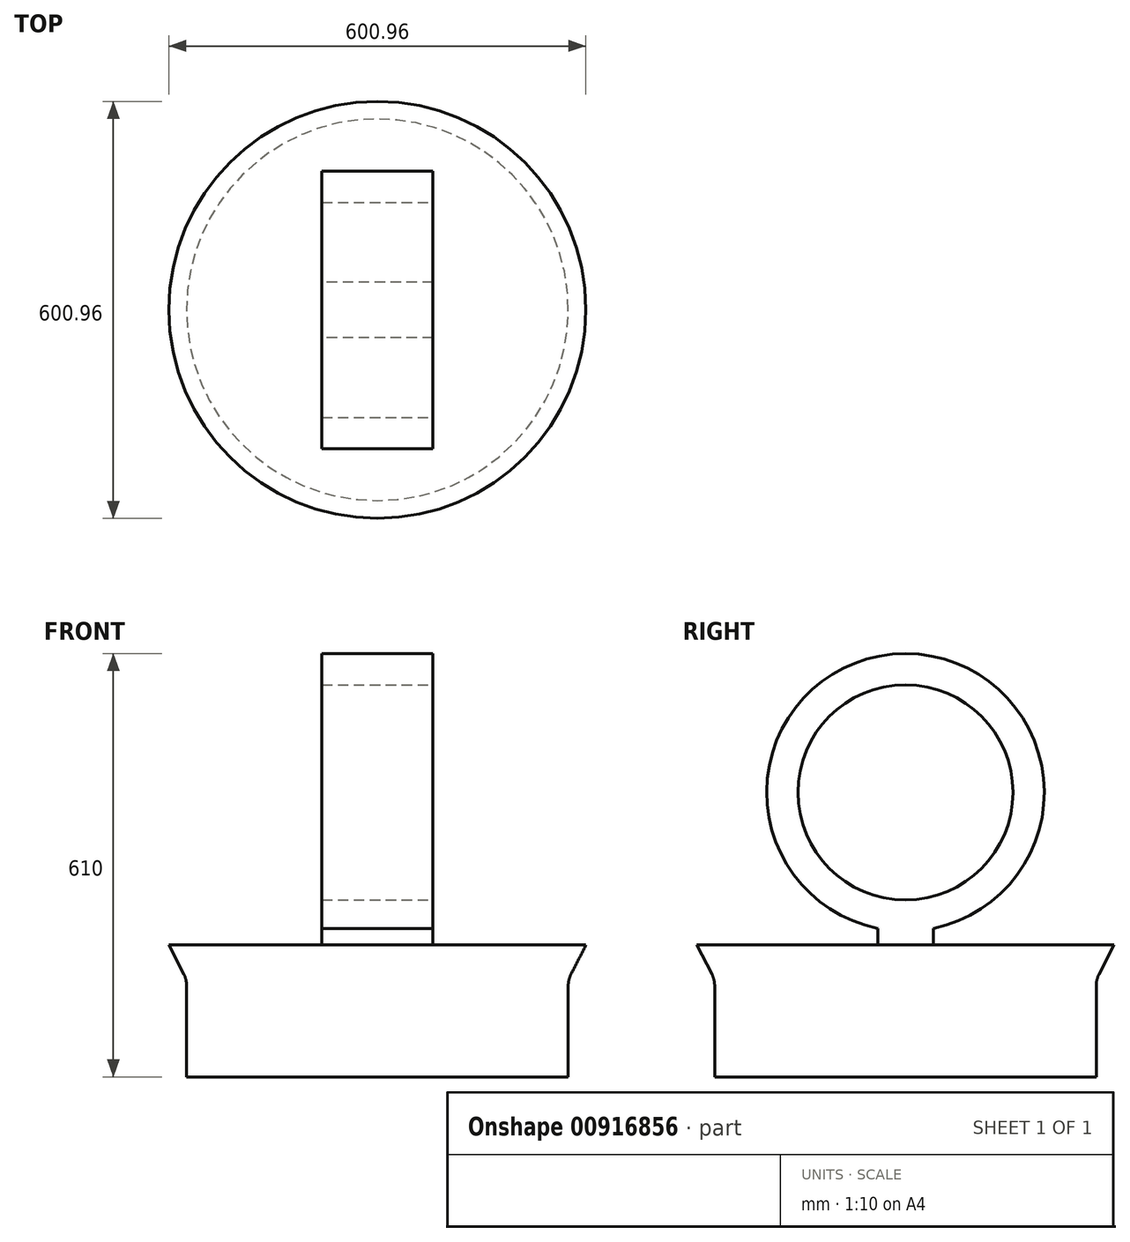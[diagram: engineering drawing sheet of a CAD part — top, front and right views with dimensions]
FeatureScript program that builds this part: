
annotation { "Feature Type Name" : "Feature", "Feature Type Description" : "" }
export const myFeature = defineFeature(function(context is Context, id is Id, definition is map)
    precondition{}
    {
        {
            var Q0;
            Q0=qCreatedBy(makeId("Top.planeOp"),FACE);
            var sketch = newSketch(context, id + "F0", { "sketchPlane" : qUnion([Q0])});
            skCircle(sketch, "E0", {"center": v(0, 0) * mm, "radius": 275 * mm});
            skSolve(sketch);
        }
        {
            var Q0;
            Q0=qSketchRegion(id+"F0",true);
            extrude(context, id + "F1", {"entities" : qUnion([Q0]), "depth" : 140 * mm, "offsetDistance" : 25 * mm});
        }
        {
            var Q0;
            Q0=makeQuery(id+"F1.opExtrude","CAP_FACE",FACE,{"disambiguationData":[OSD([sQuery(id+"F0.wireOp",EDGE,"E0")])],"isStart":false});
            var sketch = newSketch(context, id + "F2", { "sketchPlane" : qUnion([Q0])});
            skCircle(sketch, "E1", {"center": v(0, 0) * mm, "radius": 275 * mm});
            skSolve(sketch);
        }
        {
            var Q0;
            Q0=qSketchRegion(id+"F2",true);
            extrude(context, id + "F3", {"entities" : qUnion([Q0]), "operationType" : NewBodyOperationType.ADD, "depth" : 50 * mm, "offsetDistance" : 25 * mm, "hasDraft" : true, "draftAngle" : 27 * degree});
        }
        {
            var Q0;
            Q0=makeQuery(id+"F3.boolean.opBoolean","MERGE",EDGE,{"derivedFrom":[makeQuery(id+"F1.opExtrude","CAP_EDGE",EDGE,{"disambiguationData":[OSD([sQuery(id+"F0.wireOp",EDGE,"E0")])],"isStart":false}),makeQuery(id+"F3.opExtrude","CAP_EDGE",EDGE,{"disambiguationData":[OSD([sQuery(id+"F2.wireOp",EDGE,"E1")])],"isStart":true})]});
            fillet(context, id + "F4", {"entities" : qUnion([Q0]), "radius" : 35.2 * mm, "tangentPropagation" : true, "allowEdgeOverflow" : false});
        }
        {
            var Q0;
            Q0=makeQuery(id+"F3.opExtrude","CAP_FACE",FACE,{"disambiguationData":[OSD([sQuery(id+"F2.wireOp",EDGE,"E1")])],"isStart":false});
            var sketch = newSketch(context, id + "F5", { "sketchPlane" : qUnion([Q0])});
            skLineSegment(sketch, "E2.bottom", {"start": v(80, 40) * mm, "end": v(-80, 40) * mm});
            skLineSegment(sketch, "E2.top", {"start": v(80, -40) * mm, "end": v(-80, -40) * mm});
            skLineSegment(sketch, "E2.left", {"start": v(80, 40) * mm, "end": v(80, -40) * mm});
            skLineSegment(sketch, "E2.right", {"start": v(-80, 40) * mm, "end": v(-80, -40) * mm});
            skPoint(sketch, "E2.middle", {"position": v(0, 0) * mm});
            skSolve(sketch);
        }
        {
            var Q0;
            Q0 = qSketchRegion(id + "F5", true);
            extrude(context, id + "F6", {"entities" : qUnion([Q0]), "operationType" : NewBodyOperationType.ADD, "depth" : 65 * mm, "offsetDistance" : 25 * mm});
        }
        {
            var Q0;
            Q0=qCreatedBy(makeId("Front.planeOp"),FACE);
            var sketch = newSketch(context, id + "F7", { "sketchPlane" : qUnion([Q0])});
            skLineSegment(sketch, "E3.bottom", {"start": v(-80, 255) * mm, "end": v(80, 255) * mm});
            skLineSegment(sketch, "E3.top", {"start": v(-80, 210) * mm, "end": v(80, 210) * mm});
            skLineSegment(sketch, "E3.left", {"start": v(-80, 255) * mm, "end": v(-80, 210) * mm});
            skLineSegment(sketch, "E3.right", {"start": v(80, 255) * mm, "end": v(80, 210) * mm});
            skSolve(sketch);
        }
        {
            var Q0;
            Q0=qCreatedBy(makeId("Right.planeOp"),FACE);
            var sketch = newSketch(context, id + "F8", { "sketchPlane" : qUnion([Q0])});
            skLineSegment(sketch, "E4", {"start": v(0, 0) * mm, "end": v(0, 210) * mm});
            skCircle(sketch, "E5", {"center": v(0, 410) * mm, "radius": 200 * mm});
            skSolve(sketch);
        }
        {
            var Q0;
            Q0 = qSketchRegion(id + "F7", true);
            var Q1;
            Q1=sQuery(id+"F8.wireOp",EDGE,"E5");
            sweep(context, id + "F9", {"operationType" : NewBodyOperationType.ADD, "profiles" : qUnion([Q0]), "path" : qUnion([Q1])});
        }
    });
